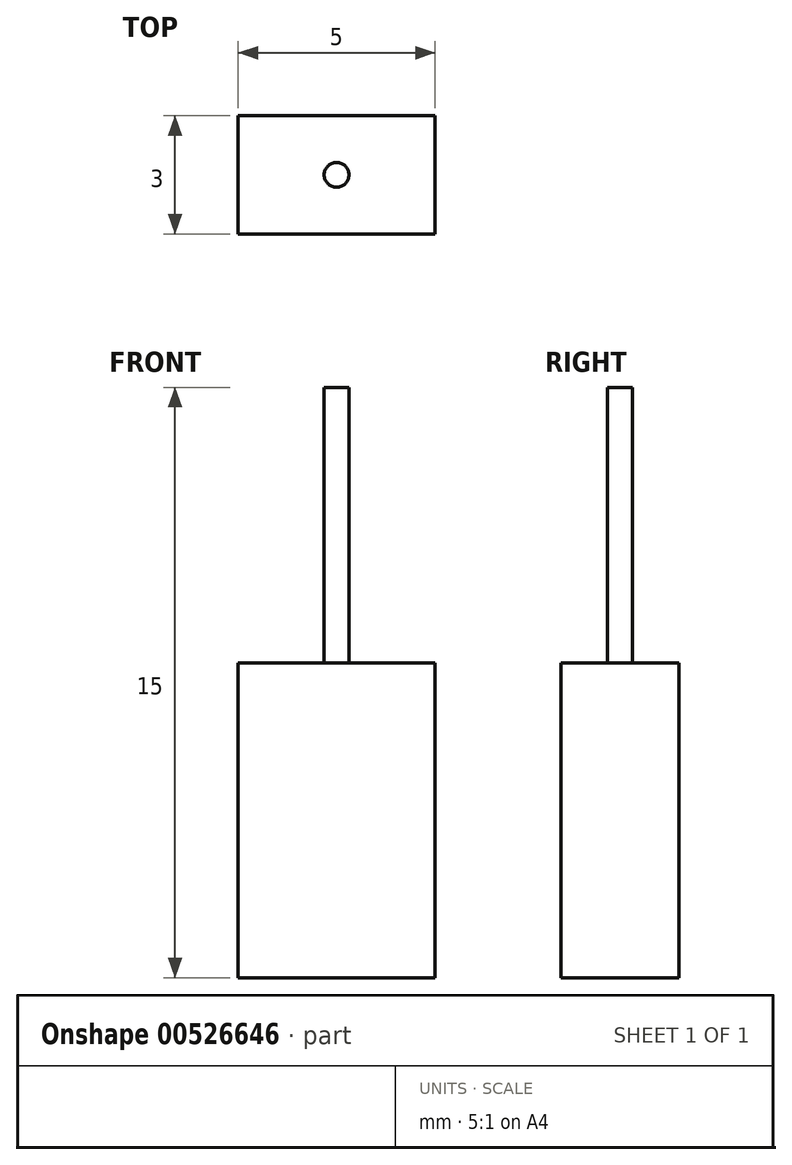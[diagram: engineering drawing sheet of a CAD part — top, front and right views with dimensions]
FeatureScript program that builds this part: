
annotation { "Feature Type Name" : "Feature", "Feature Type Description" : "" }
export const myFeature = defineFeature(function(context is Context, id is Id, definition is map)
    precondition{}
    {
        {
            var Q0;
            Q0=qCreatedBy(makeId("Top.planeOp"),FACE);
            var sketch = newSketch(context, id + "F0", { "sketchPlane" : qUnion([Q0])});
            skLineSegment(sketch, "E0.bottom", {"start": v(0, 0) * mm, "end": v(5, 0) * mm});
            skLineSegment(sketch, "E0.top", {"start": v(0, -3) * mm, "end": v(5, -3) * mm});
            skLineSegment(sketch, "E0.left", {"start": v(0, 0) * mm, "end": v(0, -3) * mm});
            skLineSegment(sketch, "E0.right", {"start": v(5, 0) * mm, "end": v(5, -3) * mm});
            skSolve(sketch);
        }
        {
            var Q0;
            Q0 = qSketchRegion(id + "F0", true);
            extrude(context, id + "F1", {"entities" : qUnion([Q0]), "depth" : 8 * mm, "offsetDistance" : 25 * mm});
        }
        {
            var Q0;
            Q0=makeQuery(id+"F1.opExtrude","CAP_FACE",FACE,{"disambiguationData":[OSD([sQuery(id+"F0.wireOp",EDGE,"E0.bottom"),sQuery(id+"F0.wireOp",EDGE,"E0.top"),sQuery(id+"F0.wireOp",EDGE,"E0.left"),sQuery(id+"F0.wireOp",EDGE,"E0.right")])],"isStart":false});
            var sketch = newSketch(context, id + "F2", { "sketchPlane" : qUnion([Q0])});
            skLineSegment(sketch, "E1", {"start": v(0, -3) * mm, "end": v(5, 0) * mm, "construction": true});
            skLineSegment(sketch, "E2", {"start": v(0, 0) * mm, "end": v(5, -3) * mm, "construction": true});
            skCircle(sketch, "E3", {"center": v(2.5, -1.5) * mm, "radius": 0.31 * mm});
            skSolve(sketch);
        }
        {
            var Q0;
            Q0 = qSketchRegion(id + "F2", true);
            var Q1;
            Q1=sQuery(id+"F2.wireOp",EDGE,"E3");
            extrude(context, id + "F3", {"entities" : qUnion([Q0]), "operationType" : NewBodyOperationType.ADD, "surfaceEntities" : qUnion([Q1]), "depth" : 7 * mm, "offsetDistance" : 25 * mm});
        }
    });
